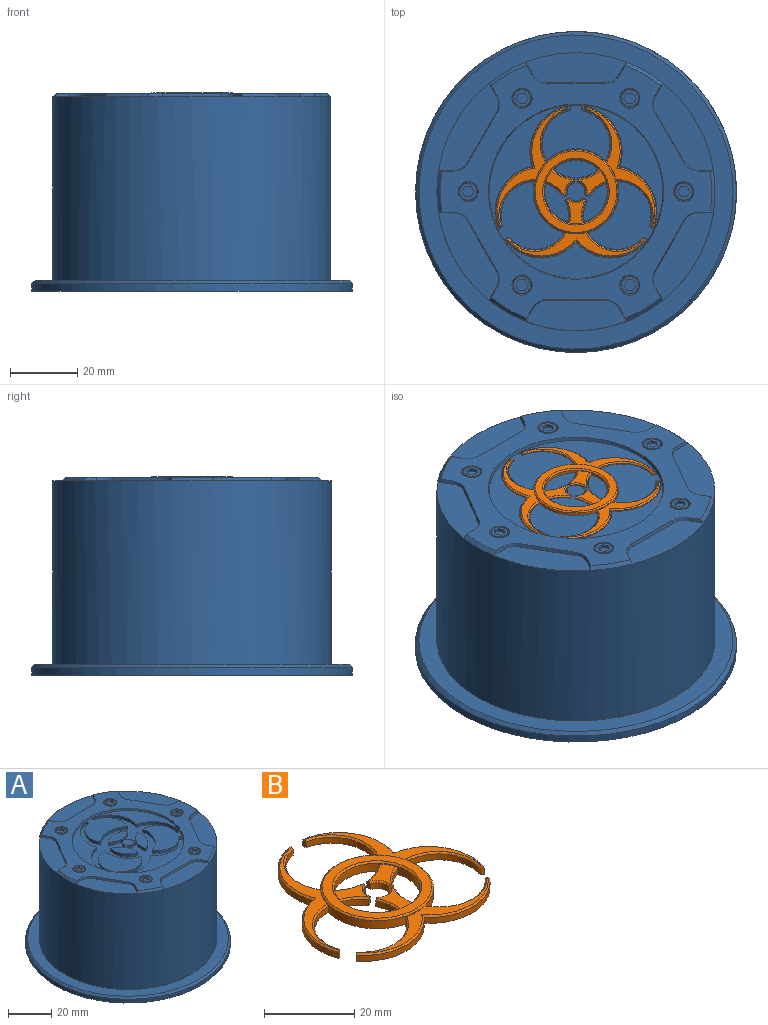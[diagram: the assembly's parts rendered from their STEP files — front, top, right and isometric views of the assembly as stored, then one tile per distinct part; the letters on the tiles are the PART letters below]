
ASSEMBLY  parts=2 mates=1
PART A: 160 faces, bbox 95.3x95.3x58.7 mm
  f0: plane 51.46x51.46mm, normal (0,0,1), area 1182.5mm2, adj f52,f121,f122,f123,f124,f128,f129,f130
  f1: plane 80.55x75.01mm, normal (0,0,1), area 1626.4mm2, adj f2,f3,f4,f5,f6,f7,f16,f17
  f2: cone r=41.27mm half-angle=45deg, axis (0,0,-1), area 17.5mm2, adj f1,f13,f26,f46
  f3: cone r=41.27mm half-angle=45deg, axis (0,0,-1), area 17.5mm2, adj f1,f13,f40,f50
  f4: cone r=41.27mm half-angle=45deg, axis (0,0,-1), area 17.5mm2, adj f1,f13,f34,f44
  f5: cone r=41.27mm half-angle=45deg, axis (0,0,-1), area 17.5mm2, adj f1,f13,f28,f38
  f6: cone r=41.27mm half-angle=45deg, axis (0,0,-1), area 17.5mm2, adj f1,f13,f20,f22
  f7: cone r=41.27mm half-angle=45deg, axis (0,0,-1), area 17.5mm2, adj f1,f13,f16,f32
  f8: plane 1.75x1.75mm, normal (0,0,-1), area 2.4mm2, adj f15
  f9: cylinder r=38.88mm len=77.75mm, axis (0,0,-1), area 4085.2mm2, adj f10,f15
  f10: plane 95.25x95.25mm, normal (0,0,-1), area 2377.8mm2, adj f9,f11
  f11: cylinder r=47.62mm len=95.25mm, axis (0,0,-1), area 650.8mm2, adj f10,f14
  f12: plane 93.25x93.25mm, normal (0,0,1), area 1477.4mm2, adj f13,f14
  f13: cylinder r=41.27mm len=82.55mm, axis (0,0,-1), area 14146.9mm2, adj f2,f3,f4,f5,f6,f7,f12,f21
  f14: cone r=47.62mm half-angle=45deg, axis (0,0,-1), area 418.7mm2, adj f11,f12
  f15: cone r=0.88mm half-angle=45deg, axis (0,0,-1), area 6711mm2, adj f8,f9
  f16: plane 3.98x2.22mm, normal (0.84,0.48,0.26), area 4.1mm2, adj f1,f7,f17,f21
  f17: cone r=5mm half-angle=15deg, axis (0,0,1), area 5.3mm2, adj f1,f16,f18,f21
  f18: plane 17.23x1mm, normal (0,0.97,0.26), area 17.8mm2, adj f1,f17,f19,f21
  f19: cone r=5mm half-angle=15deg, axis (0,0,1), area 5.3mm2, adj f1,f18,f20,f21
  f20: plane 3.98x2.22mm, normal (-0.84,0.48,0.26), area 4.1mm2, adj f1,f6,f19,f21
  f21: plane 29.86x9.01mm, normal (0,0,1), area 216.9mm2, adj f13,f16,f17,f18,f19,f20
  f22: plane 3.85x2.45mm, normal (0.84,-0.48,0.26), area 4.1mm2, adj f1,f6,f23,f27
  f23: cone r=5mm half-angle=15deg, axis (0,0,1), area 5.3mm2, adj f1,f22,f24,f27
  f24: plane 15.05x8.85mm, normal (0.84,0.48,0.26), area 17.8mm2, adj f1,f23,f25,f27
  f25: cone r=5mm half-angle=15deg, axis (0,0,1), area 5.3mm2, adj f1,f24,f26,f27
  f26: plane 4.44x1mm, normal (0,0.97,0.26), area 4.1mm2, adj f1,f2,f25,f27
  f27: plane 25.86x17.79mm, normal (0,0,1), area 216.9mm2, adj f13,f22,f23,f24,f25,f26
  f28: plane 4.44x1mm, normal (0,0.97,0.26), area 4.1mm2, adj f1,f5,f29,f33
  f29: cone r=5mm half-angle=15deg, axis (0,0,1), area 5.3mm2, adj f1,f28,f30,f33
  f30: plane 15.05x8.85mm, normal (-0.84,0.48,0.26), area 17.8mm2, adj f1,f29,f31,f33
  f31: cone r=5mm half-angle=15deg, axis (0,0,1), area 5.3mm2, adj f1,f30,f32,f33
  f32: plane 3.85x2.45mm, normal (-0.84,-0.48,0.26), area 4.1mm2, adj f1,f7,f31,f33
  f33: plane 25.86x17.79mm, normal (0,0,1), area 216.9mm2, adj f13,f28,f29,f30,f31,f32
  f34: plane 3.85x2.45mm, normal (-0.84,0.48,0.26), area 4.1mm2, adj f1,f4,f35,f39
  f35: cone r=5mm half-angle=15deg, axis (0,0,1), area 5.3mm2, adj f1,f34,f36,f39
  f36: plane 15.05x8.85mm, normal (-0.84,-0.48,0.26), area 17.8mm2, adj f1,f35,f37,f39
  f37: cone r=5mm half-angle=15deg, axis (0,0,1), area 5.3mm2, adj f1,f36,f38,f39
  f38: plane 4.44x1mm, normal (0,-0.97,0.26), area 4.1mm2, adj f1,f5,f37,f39
  f39: plane 25.86x17.79mm, normal (0,0,1), area 216.9mm2, adj f13,f34,f35,f36,f37,f38
  f40: plane 3.98x2.22mm, normal (-0.84,-0.48,0.26), area 4.1mm2, adj f1,f3,f41,f45
  f41: cone r=5mm half-angle=15deg, axis (0,0,1), area 5.3mm2, adj f1,f40,f42,f45
  f42: plane 17.23x1mm, normal (0,-0.97,0.26), area 17.8mm2, adj f1,f41,f43,f45
  f43: cone r=5mm half-angle=15deg, axis (0,0,1), area 5.3mm2, adj f1,f42,f44,f45
  f44: plane 3.98x2.22mm, normal (0.84,-0.48,0.26), area 4.1mm2, adj f1,f4,f43,f45
  f45: plane 29.86x9.01mm, normal (0,0,1), area 216.9mm2, adj f13,f40,f41,f42,f43,f44
  f46: plane 4.44x1mm, normal (0,-0.97,0.26), area 4.1mm2, adj f1,f2,f47,f51
  f47: cone r=5mm half-angle=15deg, axis (0,0,1), area 5.3mm2, adj f1,f46,f48,f51
  f48: plane 15.05x8.85mm, normal (0.84,-0.48,0.26), area 17.8mm2, adj f1,f47,f49,f51
  f49: cone r=5mm half-angle=15deg, axis (0,0,1), area 5.3mm2, adj f1,f48,f50,f51
  f50: plane 3.85x2.45mm, normal (0.84,0.48,0.26), area 4.1mm2, adj f1,f3,f49,f51
  f51: plane 25.86x17.79mm, normal (0,0,1), area 216.9mm2, adj f13,f46,f47,f48,f49,f50
  f52: cone r=26mm half-angle=15deg, axis (0,0,1), area 168.3mm2, adj f0,f1
  f53: cone r=3mm half-angle=15deg, axis (0,0,1), area 18.6mm2, adj f1,f54
  f54: plane 5.46x5.46mm, normal (0,0,1), area 3.8mm2, adj f53,f116
  f55: cone r=3mm half-angle=15deg, axis (0,0,1), area 18.6mm2, adj f1,f56
  f56: plane 5.46x5.46mm, normal (0,0,1), area 3.8mm2, adj f55,f71
  f57: cone r=3mm half-angle=15deg, axis (0,0,1), area 18.6mm2, adj f1,f58
  f58: plane 5.46x5.46mm, normal (0,0,1), area 3.8mm2, adj f57,f80
  f59: cone r=3mm half-angle=15deg, axis (0,0,1), area 18.6mm2, adj f1,f60
  f60: plane 5.46x5.46mm, normal (0,0,1), area 3.8mm2, adj f59,f89
  f61: cone r=3mm half-angle=15deg, axis (0,0,1), area 18.6mm2, adj f1,f62
  f62: plane 5.46x5.46mm, normal (0,0,1), area 3.8mm2, adj f61,f107
  f63: cone r=3mm half-angle=15deg, axis (0,0,1), area 18.6mm2, adj f1,f64
  f64: plane 5.46x5.46mm, normal (0,0,1), area 3.8mm2, adj f63,f98
  f65: plane 1.79x1mm, normal (0,1,0), area 1.8mm2, adj f66,f70,f72,f73
  f66: plane 1.55x1mm, normal (0.87,0.5,0), area 1.8mm2, adj f65,f67,f72,f73
  f67: plane 1.55x1mm, normal (0.87,-0.5,0), area 1.8mm2, adj f66,f68,f72,f73
  f68: plane 1.79x1mm, normal (0,-1,0), area 1.8mm2, adj f67,f69,f72,f73
  f69: plane 1.55x1mm, normal (-0.87,-0.5,0), area 1.8mm2, adj f68,f70,f72,f73
  f70: plane 1.55x1mm, normal (-0.87,0.5,0), area 1.8mm2, adj f65,f69,f72,f73
  f71: cylinder r=2.5mm len=5mm, axis (0,0,-1), area 15.7mm2, adj f56,f72
  f72: plane 5x5mm, normal (0,0,1), area 11.3mm2, adj f65,f66,f67,f68,f69,f70,f71
  f73: plane 3.58x3.1mm, normal (0,0,1), area 8.3mm2, adj f65,f66,f67,f68,f69,f70
  f74: plane 1.79x1mm, normal (0,1,0), area 1.8mm2, adj f75,f79,f81,f82
  f75: plane 1.55x1mm, normal (0.87,0.5,0), area 1.8mm2, adj f74,f76,f81,f82
  f76: plane 1.55x1mm, normal (0.87,-0.5,0), area 1.8mm2, adj f75,f77,f81,f82
  f77: plane 1.79x1mm, normal (0,-1,0), area 1.8mm2, adj f76,f78,f81,f82
  f78: plane 1.55x1mm, normal (-0.87,-0.5,0), area 1.8mm2, adj f77,f79,f81,f82
  f79: plane 1.55x1mm, normal (-0.87,0.5,0), area 1.8mm2, adj f74,f78,f81,f82
  f80: cylinder r=2.5mm len=5mm, axis (0,0,-1), area 15.7mm2, adj f58,f81
  f81: plane 5x5mm, normal (0,0,1), area 11.3mm2, adj f74,f75,f76,f77,f78,f79,f80
  f82: plane 3.58x3.1mm, normal (0,0,1), area 8.3mm2, adj f74,f75,f76,f77,f78,f79
  f83: plane 1.55x1mm, normal (-0.87,0.5,0), area 1.8mm2, adj f84,f88,f90,f91
  f84: plane 1.79x1mm, normal (0,1,0), area 1.8mm2, adj f83,f85,f90,f91
  f85: plane 1.55x1mm, normal (0.87,0.5,0), area 1.8mm2, adj f84,f86,f90,f91
  f86: plane 1.55x1mm, normal (0.87,-0.5,0), area 1.8mm2, adj f85,f87,f90,f91
  f87: plane 1.79x1mm, normal (0,-1,0), area 1.8mm2, adj f86,f88,f90,f91
  f88: plane 1.55x1mm, normal (-0.87,-0.5,0), area 1.8mm2, adj f83,f87,f90,f91
  f89: cylinder r=2.5mm len=5mm, axis (0,0,-1), area 15.7mm2, adj f60,f90
  f90: plane 5x5mm, normal (0,0,1), area 11.3mm2, adj f83,f84,f85,f86,f87,f88,f89
  f91: plane 3.58x3.1mm, normal (0,0,1), area 8.3mm2, adj f83,f84,f85,f86,f87,f88
  f92: plane 1.55x1mm, normal (-0.87,-0.5,0), area 1.8mm2, adj f93,f97,f99,f100
  f93: plane 1.55x1mm, normal (-0.87,0.5,0), area 1.8mm2, adj f92,f94,f99,f100
  f94: plane 1.79x1mm, normal (0,1,0), area 1.8mm2, adj f93,f95,f99,f100
  f95: plane 1.55x1mm, normal (0.87,0.5,0), area 1.8mm2, adj f94,f96,f99,f100
  f96: plane 1.55x1mm, normal (0.87,-0.5,0), area 1.8mm2, adj f95,f97,f99,f100
  f97: plane 1.79x1mm, normal (0,-1,0), area 1.8mm2, adj f92,f96,f99,f100
  f98: cylinder r=2.5mm len=5mm, axis (0,0,-1), area 15.7mm2, adj f64,f99
  f99: plane 5x5mm, normal (0,0,1), area 11.3mm2, adj f92,f93,f94,f95,f96,f97,f98
  f100: plane 3.58x3.1mm, normal (0,0,1), area 8.3mm2, adj f92,f93,f94,f95,f96,f97
  f101: plane 1.79x1mm, normal (0,-1,0), area 1.8mm2, adj f102,f106,f108,f109
  f102: plane 1.55x1mm, normal (-0.87,-0.5,0), area 1.8mm2, adj f101,f103,f108,f109
  f103: plane 1.55x1mm, normal (-0.87,0.5,0), area 1.8mm2, adj f102,f104,f108,f109
  f104: plane 1.79x1mm, normal (0,1,0), area 1.8mm2, adj f103,f105,f108,f109
  f105: plane 1.55x1mm, normal (0.87,0.5,0), area 1.8mm2, adj f104,f106,f108,f109
  f106: plane 1.55x1mm, normal (0.87,-0.5,0), area 1.8mm2, adj f101,f105,f108,f109
  f107: cylinder r=2.5mm len=5mm, axis (0,0,-1), area 15.7mm2, adj f62,f108
  f108: plane 5x5mm, normal (0,0,1), area 11.3mm2, adj f101,f102,f103,f104,f105,f106,f107
  f109: plane 3.58x3.1mm, normal (0,0,1), area 8.3mm2, adj f101,f102,f103,f104,f105,f106
  f110: plane 1.55x1mm, normal (0.87,-0.5,0), area 1.8mm2, adj f111,f115,f117,f118
  f111: plane 1.79x1mm, normal (0,-1,0), area 1.8mm2, adj f110,f112,f117,f118
  f112: plane 1.55x1mm, normal (-0.87,-0.5,0), area 1.8mm2, adj f111,f113,f117,f118
  f113: plane 1.55x1mm, normal (-0.87,0.5,0), area 1.8mm2, adj f112,f114,f117,f118
  f114: plane 1.79x1mm, normal (0,1,0), area 1.8mm2, adj f113,f115,f117,f118
  f115: plane 1.55x1mm, normal (0.87,0.5,0), area 1.8mm2, adj f110,f114,f117,f118
  f116: cylinder r=2.5mm len=5mm, axis (0,0,-1), area 15.7mm2, adj f54,f117
  f117: plane 5x5mm, normal (0,0,1), area 11.3mm2, adj f110,f111,f112,f113,f114,f115,f116
  f118: plane 3.58x3.1mm, normal (0,0,1), area 8.3mm2, adj f110,f111,f112,f113,f114,f115
  f119: cylinder r=9.25mm len=11.29mm, axis (0,0,-1), area 25.3mm2, adj f134,f146,f152,f159
  f120: cylinder r=9.25mm len=13.03mm, axis (0,0,-1), area 25.3mm2, adj f132,f134,f141,f159
  f121: cylinder r=12.75mm len=15.13mm, axis (0,0,-1), area 33.7mm2, adj f0,f134,f138,f148
  f122: cylinder r=12.75mm len=17.47mm, axis (0,0,-1), area 33.7mm2, adj f0,f124,f134,f137
  f123: cylinder r=10mm len=13.41mm, axis (0,0,-1), area 33.3mm2, adj f0,f128,f134,f136
  f124: cylinder r=10mm len=14.71mm, axis (0,0,-1), area 33.3mm2, adj f0,f122,f131,f134
  f125: cylinder r=2.65mm len=3.41mm, axis (0,0,-1), area 7.8mm2, adj f126,f133,f134,f159
  f126: plane 1.75x1.36mm, normal (0.5,0.87,0), area 2.8mm2, adj f125,f127,f134,f159
  f127: cylinder r=10mm len=5.06mm, axis (0,0,-1), area 11.5mm2, adj f126,f134,f135,f159
  f128: plane 1.75x1.34mm, normal (0.5,0.87,0), area 2.7mm2, adj f0,f123,f129,f134
  f129: cylinder r=13.75mm len=18.78mm, axis (0,0,-1), area 42.5mm2, adj f0,f128,f130,f134
  f130: cylinder r=13.75mm len=18.01mm, axis (0,0,-1), area 42.5mm2, adj f0,f129,f131,f134
  f131: plane 1.75x1.54mm, normal (1,0,0), area 2.7mm2, adj f0,f124,f130,f134
  f132: cylinder r=10mm len=5.97mm, axis (0,0,-1), area 11.5mm2, adj f120,f133,f134,f159
  f133: plane 1.75x1.57mm, normal (1,0,0), area 2.8mm2, adj f125,f132,f134,f159
  f134: plane 48.11x45.24mm, normal (0,0,1), area 733.6mm2, adj f119,f120,f121,f122,f123,f124,f125,f126
  f135: cylinder r=9.25mm len=11.29mm, axis (0,0,-1), area 25.3mm2, adj f127,f134,f157,f159
  f136: cylinder r=12.75mm len=15.13mm, axis (0,0,-1), area 33.7mm2, adj f0,f123,f134,f149
  f137: cylinder r=10mm len=14.71mm, axis (0,0,-1), area 33.3mm2, adj f0,f122,f134,f142
  f138: cylinder r=10mm len=13.41mm, axis (0,0,-1), area 33.3mm2, adj f0,f121,f134,f145
  f139: cylinder r=2.65mm len=3.41mm, axis (0,0,-1), area 7.8mm2, adj f134,f140,f147,f159
  f140: plane 1.75x1.57mm, normal (-1,0,0), area 2.8mm2, adj f134,f139,f141,f159
  f141: cylinder r=10mm len=5.97mm, axis (0,0,-1), area 11.5mm2, adj f120,f134,f140,f159
  f142: plane 1.75x1.54mm, normal (-1,0,0), area 2.7mm2, adj f0,f134,f137,f143
  f143: cylinder r=13.75mm len=18.01mm, axis (0,0,-1), area 42.5mm2, adj f0,f134,f142,f144
  f144: cylinder r=13.75mm len=18.78mm, axis (0,0,-1), area 42.5mm2, adj f0,f134,f143,f145
  f145: plane 1.75x1.34mm, normal (-0.5,0.87,0), area 2.7mm2, adj f0,f134,f138,f144
  f146: cylinder r=10mm len=5.06mm, axis (0,0,-1), area 11.5mm2, adj f119,f134,f147,f159
  f147: plane 1.75x1.36mm, normal (-0.5,0.87,0), area 2.8mm2, adj f134,f139,f146,f159
  f148: cylinder r=10mm len=16.23mm, axis (0,0,-1), area 33.3mm2, adj f0,f121,f134,f153
  f149: cylinder r=10mm len=16.23mm, axis (0,0,-1), area 33.3mm2, adj f0,f134,f136,f156
  f150: cylinder r=2.65mm len=3.94mm, axis (0,0,-1), area 7.8mm2, adj f134,f151,f158,f159
  f151: plane 1.75x1.36mm, normal (0.5,-0.87,0), area 2.8mm2, adj f134,f150,f152,f159
  f152: cylinder r=10mm len=6.37mm, axis (0,0,-1), area 11.5mm2, adj f119,f134,f151,f159
  f153: plane 1.75x1.34mm, normal (0.5,-0.87,0), area 2.7mm2, adj f0,f134,f148,f154
  f154: cylinder r=13.75mm len=21.24mm, axis (0,0,-1), area 42.5mm2, adj f0,f134,f153,f155
  f155: cylinder r=13.75mm len=21.24mm, axis (0,0,-1), area 42.5mm2, adj f0,f134,f154,f156
  f156: plane 1.75x1.34mm, normal (-0.5,-0.87,0), area 2.7mm2, adj f0,f134,f149,f155
  f157: cylinder r=10mm len=6.37mm, axis (0,0,-1), area 11.5mm2, adj f134,f135,f158,f159
  f158: plane 1.75x1.36mm, normal (-0.5,-0.87,0), area 2.8mm2, adj f134,f150,f157,f159
  f159: plane 18.5x18.18mm, normal (0,0,1), area 164mm2, adj f119,f120,f125,f126,f127,f132,f133,f135
PART B: 66 faces, bbox 47.6x44.7x2.6 mm
  f0: cylinder r=10.25mm len=13.54mm, axis (0,0,-1), area 31.4mm2, adj f6,f13,f15,f45
  f1: cylinder r=10.25mm len=15.32mm, axis (0,0,-1), area 31.4mm2, adj f9,f13,f15,f44
  f2: plane 8.19x7.33mm, normal (0,0,1), area 23.5mm2, adj f4,f11,f14,f51,f52,f53
  f3: cylinder r=2.9mm len=3.49mm, axis (0,0,-1), area 7.1mm2, adj f4,f11,f13,f53
  f4: plane 2.01x1mm, normal (-0.5,-0.87,0), area 2.1mm2, adj f2,f3,f5,f13,f51,f53
  f5: cylinder r=10.25mm len=5.31mm, axis (0,0,-1), area 10.8mm2, adj f4,f13,f14,f51
  f6: plane 2x0.91mm, normal (-0.5,-0.87,0), area 1.9mm2, adj f0,f7,f12,f13,f45,f58
  f7: cylinder r=13.5mm len=18.23mm, axis (0,0,-1), area 38.2mm2, adj f6,f8,f13,f58
  f8: cylinder r=13.5mm len=17.92mm, axis (0,0,-1), area 38.2mm2, adj f7,f9,f13,f59
  f9: plane 2x1.05mm, normal (-1,0,0), area 1.9mm2, adj f1,f8,f12,f13,f44,f59
  f10: cylinder r=10.25mm len=6.08mm, axis (0,0,-1), area 10.8mm2, adj f11,f13,f14,f52
  f11: plane 2.01x1.15mm, normal (-1,0,0), area 2.1mm2, adj f2,f3,f10,f13,f52,f53
  f12: plane 35.54x21.41mm, normal (0,0,1), area 73.4mm2, adj f6,f9,f15,f44,f45,f58,f59
  f13: plane 47.61x44.7mm, normal (0,0,-1), area 625.5mm2, adj f0,f1,f3,f4,f5,f6,f7,f8
  f14: cylinder r=9.5mm len=19mm, axis (0,0,-1), area 104.7mm2, adj f2,f5,f10,f13,f18,f21,f26,f31
  f15: cylinder r=12.5mm len=25mm, axis (0,0,-1), area 133.2mm2, adj f0,f1,f12,f13,f16,f17,f28,f29
  f16: cylinder r=10.25mm len=15.32mm, axis (0,0,-1), area 31.4mm2, adj f13,f15,f22,f43
  f17: cylinder r=10.25mm len=13.54mm, axis (0,0,-1), area 31.4mm2, adj f13,f15,f25,f48
  f18: plane 8.19x7.33mm, normal (0,0,1), area 23.5mm2, adj f14,f20,f27,f55,f56,f57
  f19: cylinder r=2.9mm len=3.49mm, axis (0,0,-1), area 7.1mm2, adj f13,f20,f27,f55
  f20: plane 2.01x1.15mm, normal (1,0,0), area 2.1mm2, adj f13,f18,f19,f21,f55,f56
  f21: cylinder r=10.25mm len=6.08mm, axis (0,0,-1), area 10.8mm2, adj f13,f14,f20,f56
  f22: plane 2x1.05mm, normal (1,0,0), area 1.9mm2, adj f13,f16,f23,f28,f43,f63
  f23: cylinder r=13.5mm len=17.92mm, axis (0,0,-1), area 38.2mm2, adj f13,f22,f24,f63
  f24: cylinder r=13.5mm len=18.23mm, axis (0,0,-1), area 38.2mm2, adj f13,f23,f25,f62
  f25: plane 2x0.91mm, normal (0.5,-0.87,0), area 1.9mm2, adj f13,f17,f24,f28,f48,f62
  f26: cylinder r=10.25mm len=5.31mm, axis (0,0,-1), area 10.8mm2, adj f13,f14,f27,f57
  f27: plane 2.01x1mm, normal (0.5,-0.87,0), area 2.1mm2, adj f13,f18,f19,f26,f55,f57
  f28: plane 35.54x21.41mm, normal (0,0,1), area 73.4mm2, adj f15,f22,f25,f43,f48,f62,f63
  f29: cylinder r=10.25mm len=16.66mm, axis (0,0,-1), area 31.4mm2, adj f13,f15,f35,f47
  f30: cylinder r=10.25mm len=16.66mm, axis (0,0,-1), area 31.4mm2, adj f13,f15,f38,f46
  f31: plane 7.21x5.31mm, normal (0,0,1), area 23.5mm2, adj f14,f33,f40,f49,f50,f54
  f32: cylinder r=2.9mm len=4.03mm, axis (0,0,-1), area 7.1mm2, adj f13,f33,f40,f54
  f33: plane 2.01x1mm, normal (-0.5,0.87,0), area 2.1mm2, adj f13,f31,f32,f34,f49,f54
  f34: cylinder r=10.25mm len=6.58mm, axis (0,0,-1), area 10.8mm2, adj f13,f14,f33,f49
  f35: plane 2x0.91mm, normal (-0.5,0.87,0), area 1.9mm2, adj f13,f29,f36,f41,f47,f60
  f36: cylinder r=13.5mm len=20.87mm, axis (0,0,-1), area 38.2mm2, adj f13,f35,f37,f60
  f37: cylinder r=13.5mm len=20.87mm, axis (0,0,-1), area 38.2mm2, adj f13,f36,f38,f61
  f38: plane 2x0.91mm, normal (0.5,0.87,0), area 1.9mm2, adj f13,f30,f37,f41,f46,f61
  f39: cylinder r=10.25mm len=6.58mm, axis (0,0,-1), area 10.8mm2, adj f13,f14,f40,f50
  f40: plane 2.01x1mm, normal (0.5,0.87,0), area 2.1mm2, adj f13,f31,f32,f39,f50,f54
  f41: plane 41.04x6.89mm, normal (0,0,1), area 73.4mm2, adj f15,f35,f38,f46,f47,f60,f61
  f42: plane 24.2x24.2mm, normal (0,0,1), area 152.1mm2, adj f64,f65
  f43: cone r=10.65mm half-angle=45deg, axis (0,0,1), area 11.4mm2, adj f15,f16,f22,f28
  f44: cone r=10.25mm half-angle=45deg, axis (0,0,1), area 11.4mm2, adj f1,f9,f12,f15
  f45: cone r=10.65mm half-angle=45deg, axis (0,0,1), area 11.4mm2, adj f0,f6,f12,f15
  f46: cone r=10.25mm half-angle=45deg, axis (0,0,1), area 11.4mm2, adj f15,f30,f38,f41
  f47: cone r=10.65mm half-angle=45deg, axis (0,0,1), area 11.4mm2, adj f15,f29,f35,f41
  f48: cone r=10.25mm half-angle=45deg, axis (0,0,1), area 11.4mm2, adj f15,f17,f25,f28
  f49: cone r=10.65mm half-angle=45deg, axis (0,0,1), area 3.9mm2, adj f14,f31,f33,f34
  f50: cone r=10.25mm half-angle=45deg, axis (0,0,1), area 3.9mm2, adj f14,f31,f39,f40
  f51: cone r=10.65mm half-angle=45deg, axis (0,0,1), area 3.9mm2, adj f2,f4,f5,f14
  f52: cone r=10.25mm half-angle=45deg, axis (0,0,1), area 3.9mm2, adj f2,f10,f11,f14
  f53: cone r=2.9mm half-angle=45deg, axis (0,0,1), area 2.8mm2, adj f2,f3,f4,f11
  f54: cone r=2.9mm half-angle=45deg, axis (0,0,1), area 2.8mm2, adj f31,f32,f33,f40
  f55: cone r=2.9mm half-angle=45deg, axis (0,0,1), area 2.8mm2, adj f18,f19,f20,f27
  f56: cone r=10.65mm half-angle=45deg, axis (0,0,1), area 3.9mm2, adj f14,f18,f20,f21
  f57: cone r=10.25mm half-angle=45deg, axis (0,0,1), area 3.9mm2, adj f14,f18,f26,f27
  f58: cone r=13.5mm half-angle=45deg, axis (0,0,-1), area 13.4mm2, adj f6,f7,f12,f59
  f59: cone r=13.1mm half-angle=45deg, axis (0,0,-1), area 13.4mm2, adj f8,f9,f12,f58
  f60: cone r=13.5mm half-angle=45deg, axis (0,0,-1), area 13.4mm2, adj f35,f36,f41,f61
  f61: cone r=13.1mm half-angle=45deg, axis (0,0,-1), area 13.4mm2, adj f37,f38,f41,f60
  f62: cone r=13.1mm half-angle=45deg, axis (0,0,-1), area 13.4mm2, adj f24,f25,f28,f63
  f63: cone r=13.5mm half-angle=45deg, axis (0,0,-1), area 13.4mm2, adj f22,f23,f28,f62
  f64: cone r=12.1mm half-angle=45deg, axis (0,0,-1), area 43.7mm2, adj f15,f42
  f65: cone r=9.5mm half-angle=45deg, axis (0,0,1), area 34.5mm2, adj f14,f42
PLACE A at identity fixed
PLACE B t=(0,0,56.22)mm
MATE fastened A.f52 <-> B.f3  axis (0,0,1) through (0,0,57.72)mm
